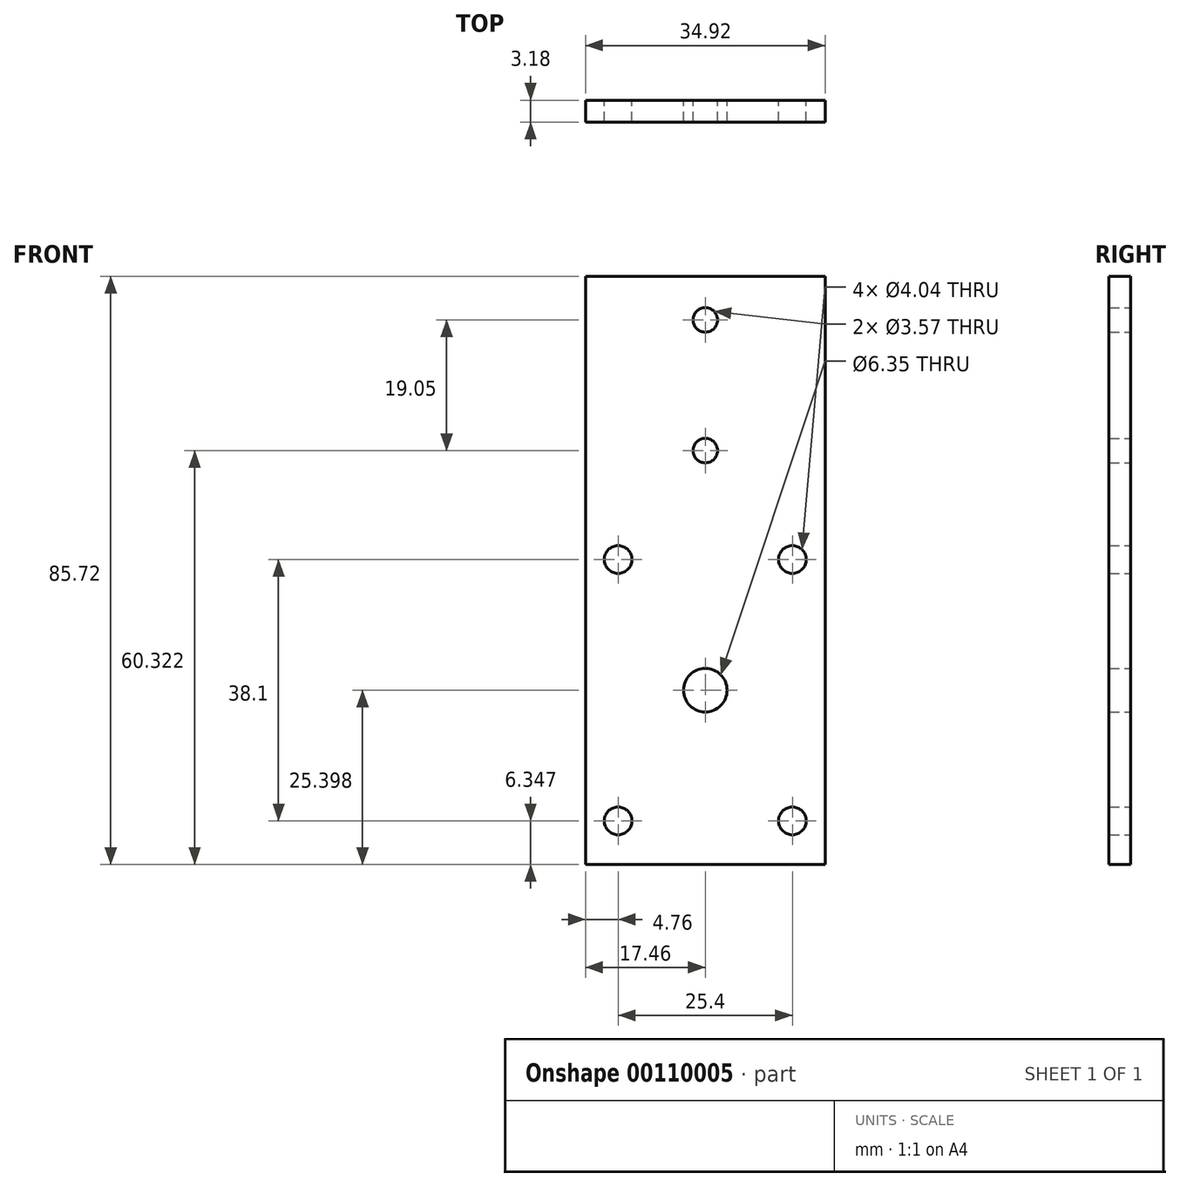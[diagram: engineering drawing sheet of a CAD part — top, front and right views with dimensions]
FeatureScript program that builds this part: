
annotation { "Feature Type Name" : "Feature", "Feature Type Description" : "" }
export const myFeature = defineFeature(function(context is Context, id is Id, definition is map)
    precondition{}
    {
        {
            var Q0;
            Q0=qCreatedBy(makeId("Front.planeOp"),FACE);
            var sketch = newSketch(context, id + "F0", { "sketchPlane" : qUnion([Q0])});
            skLineSegment(sketch, "E0.bottom", {"start": v(17.46, 42.86) * mm, "end": v(-17.46, 42.86) * mm});
            skLineSegment(sketch, "E0.top", {"start": v(17.46, -42.86) * mm, "end": v(-17.46, -42.86) * mm});
            skLineSegment(sketch, "E0.left", {"start": v(17.46, 42.86) * mm, "end": v(17.46, -42.86) * mm});
            skLineSegment(sketch, "E0.right", {"start": v(-17.46, 42.86) * mm, "end": v(-17.46, -42.86) * mm});
            skPoint(sketch, "E0.middle", {"position": v(0, 0) * mm});
            skCircle(sketch, "E1", {"center": v(-12.7, -36.51) * mm, "radius": 2.02 * mm});
            skCircle(sketch, "E2", {"center": v(-12.7, 1.59) * mm, "radius": 2.02 * mm});
            skCircle(sketch, "E3.MirrorC", {"center": v(12.7, -36.51) * mm, "radius": 2.02 * mm});
            skCircle(sketch, "E4.MirrorC", {"center": v(12.7, 1.59) * mm, "radius": 2.02 * mm});
            skCircle(sketch, "E5", {"center": v(0, -17.46) * mm, "radius": 3.18 * mm});
            skCircle(sketch, "E6", {"center": v(0, 17.46) * mm, "radius": 1.78 * mm});
            skCircle(sketch, "E7", {"center": v(0, 36.51) * mm, "radius": 1.78 * mm});
            skSolve(sketch);
        }
        {
            var Q0;
            Q0=makeQuery(id+"F0.imprint","IMPRINT",FACE,{"disambiguationData":[TD([[makeQuery(id+"F0.imprint","IMPRINT",EDGE,{"derivedFrom":sQuery(id+"F0.wireOp",EDGE,"E0.bottom")}),1.0]])]});
            extrude(context, id + "F1", {"entities" : qUnion([Q0]), "depth" : 3.17 * mm});
        }
    });
